# Revit family: Franke_Unterthekenkühleinheit_UT12_CM-A1000_FM_CM
name_source: partatom
category: Sonderausstattung
revit_build: Autodesk Revit 2015 (Build: 20140606_1530(x64)
units: mm (PartAtom-declared; Revit-internal decimal feet)

## types (2) — shared parameters
Anzahl der Nullleiter = 1
Anzahl der Schutzleiter = 1
Anzahl von Polen = 1
Aufstellgewicht = 26 kg
Bauelement = Beistellgerät Unterthekenkühleinheit UT12
Baugruppenkennzeichen = Beistellgerät Unterthekenkühleinheit UT12
Beschreibung = Beistellgerät Unterthekenkühleinheit UT12 dient zum Aufbewahren von gekühlter Milch
Breite = 340 mm  [stored 1.11549 ft]
Energieverlust nach DIN18873 = 0.783 kWh/24 h - 230 V
Hersteller = Franke
Höhe = 544 mm  [stored 1.78478 ft]
Milchvorrat = 12 l
Modell = 410880 - Unterthekenkühleinheit UT12 CM - A1000 FM CM
Netzfrequenz = 50 Hz
Netzfrequenz alternativ = 60 Hz
Sicherung = 10 A
Spannung = 230 V
Stromaufnahme = 0.72 A
Temperaturbereich = + 3° bis + 8°
Tiefe = 475 mm  [stored 1.5584 ft]
URL = http://www.franke.com
zero-valued in all types: Kosten

## per-type parameters (varying)
| type | Abdeckung Front |
| Unterthekenkühleinheit UT12 CM-A1000 FM CM(230V/black line/EU) | Franke Black |
| Unterthekenkühleinheit UT12 CM-A1000 FM CM(230V/anthrazit/EU) | Franke Anthrazit |

note: [stored X ft] marks values corroborated as IEEE doubles in the binary element streams (Revit-internal decimal feet)
